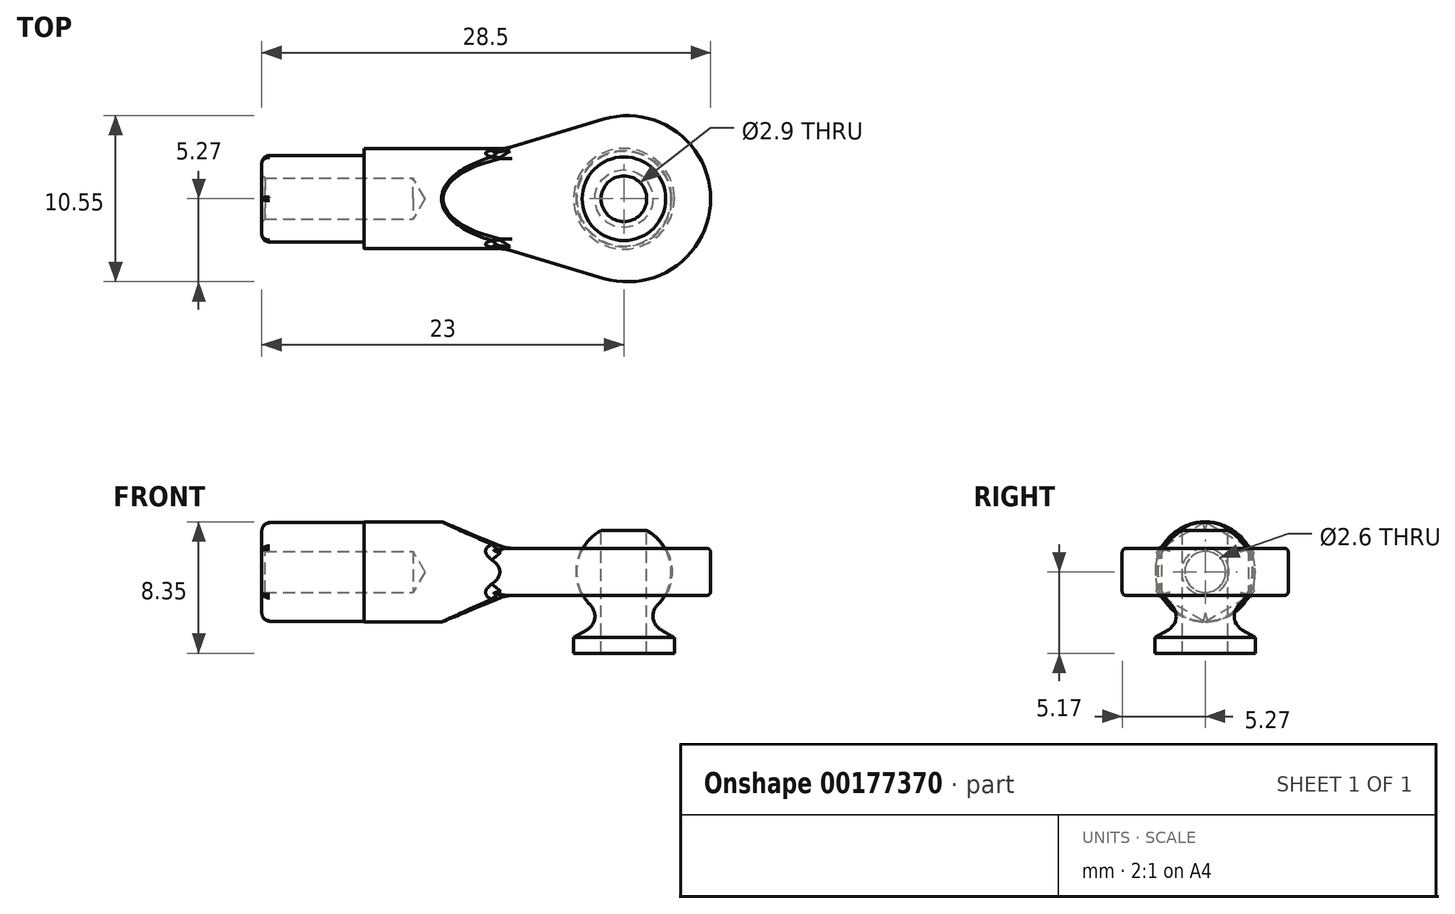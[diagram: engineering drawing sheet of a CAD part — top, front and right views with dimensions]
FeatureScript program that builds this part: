
annotation { "Feature Type Name" : "Feature", "Feature Type Description" : "" }
export const myFeature = defineFeature(function(context is Context, id is Id, definition is map)
    precondition{}
    {
        {
            var Q0;
            Q0=qCreatedBy(makeId("Right.planeOp"),FACE);
            var sketch = newSketch(context, id + "F0", { "sketchPlane" : qUnion([Q0])});
            skCircle(sketch, "E0.cCircle", {"center": v(0, 0) * mm, "radius": 2.75 * mm, "construction": true});
            skLineSegment(sketch, "E0.0", {"start": v(2.75, 1.59) * mm, "end": v(2.75, -1.59) * mm});
            skLineSegment(sketch, "E0.1", {"start": v(2.75, -1.59) * mm, "end": v(0, -3.18) * mm});
            skLineSegment(sketch, "E0.2", {"start": v(0, -3.18) * mm, "end": v(-2.75, -1.59) * mm});
            skLineSegment(sketch, "E0.3", {"start": v(-2.75, -1.59) * mm, "end": v(-2.75, 1.59) * mm});
            skLineSegment(sketch, "E0.4", {"start": v(-2.75, 1.59) * mm, "end": v(0, 3.18) * mm});
            skLineSegment(sketch, "E0.5", {"start": v(0, 3.18) * mm, "end": v(2.75, 1.59) * mm});
            skPoint(sketch, "E0.0.midPoint", {"position": v(2.75, 0) * mm});
            skSolve(sketch);
        }
        {
            var Q0;
            Q0 = qSketchRegion(id + "F0", true);
            extrude(context, id + "F1", {"entities" : qUnion([Q0]), "depth" : 6.5 * mm, "offsetDistance" : 25 * mm});
        }
        {
            var Q0;
            Q0=makeQuery(id+"F1.opExtrude","CAP_FACE",FACE,{"disambiguationData":[OSD([sQuery(id+"F0.wireOp",EDGE,"E0.0"),sQuery(id+"F0.wireOp",EDGE,"E0.1"),sQuery(id+"F0.wireOp",EDGE,"E0.2"),sQuery(id+"F0.wireOp",EDGE,"E0.3"),sQuery(id+"F0.wireOp",EDGE,"E0.4"),sQuery(id+"F0.wireOp",EDGE,"E0.5")])],"isStart":false});
            var sketch = newSketch(context, id + "F2", { "sketchPlane" : qUnion([Q0])});
            skCircle(sketch, "E1", {"center": v(0, 0) * mm, "radius": 3.18 * mm});
            skSolve(sketch);
        }
        {
            var Q0;
            Q0 = qSketchRegion(id + "F2", true);
            extrude(context, id + "F3", {"entities" : qUnion([Q0]), "operationType" : NewBodyOperationType.ADD, "depth" : 9 * mm, "offsetDistance" : 25 * mm});
        }
        {
            var Q0;
            Q0=qCreatedBy(makeId("Top.planeOp"),FACE);
            var sketch = newSketch(context, id + "F4", { "sketchPlane" : qUnion([Q0])});
            skCircle(sketch, "E2", {"center": v(23.23, 0) * mm, "radius": 5.28 * mm, "construction": true});
            skLineSegment(sketch, "E3", {"start": v(21.72, -5.05) * mm, "end": v(13.5, -2.6) * mm});
            skLineSegment(sketch, "E4", {"start": v(13.5, -2.6) * mm, "end": v(13.5, 2.6) * mm});
            skLineSegment(sketch, "E5", {"start": v(13.5, 2.6) * mm, "end": v(21.72, 5.05) * mm});
            skArc(sketch, "E6", {"start": v(21.72, -5.05) * mm, "mid": v(28.5, 0) * mm, "end": v(21.72, 5.05) * mm});
            skPoint(sketch, "E7", {"position": v(15.5, 3.2) * mm});
            skPoint(sketch, "E8", {"position": v(15.5, -3.2) * mm});
            skSolve(sketch);
        }
        {
            var Q0;
            Q0 = qSketchRegion(id + "F4", true);
            extrude(context, id + "F5", {"entities" : qUnion([Q0]), "operationType" : NewBodyOperationType.ADD, "depth" : 3 * mm, "offsetDistance" : 25 * mm, "symmetric" : true});
        }
        {
            var Q0;
            Q0=qCreatedBy(makeId("Front.planeOp"),FACE);
            var sketch = newSketch(context, id + "F6", { "sketchPlane" : qUnion([Q0])});
            skLineSegment(sketch, "E9", {"start": v(15.5, 1.5) * mm, "end": v(10.25, 3.67) * mm});
            skLineSegment(sketch, "E10", {"start": v(10.25, 3.67) * mm, "end": v(16.92, 3.67) * mm});
            skLineSegment(sketch, "E11", {"start": v(16.92, 3.67) * mm, "end": v(15.5, 1.5) * mm});
            skLineSegment(sketch, "E12", {"start": v(15.5, -1.5) * mm, "end": v(9.73, -3.9) * mm});
            skLineSegment(sketch, "E13", {"start": v(9.73, -3.9) * mm, "end": v(16.66, -3.9) * mm});
            skLineSegment(sketch, "E14", {"start": v(16.66, -3.9) * mm, "end": v(15.5, -1.5) * mm});
            skSolve(sketch);
        }
        {
            var Q0;
            Q0 = qSketchRegion(id + "F6", true);
            extrude(context, id + "F7", {"entities" : qUnion([Q0]), "operationType" : NewBodyOperationType.REMOVE, "oppositeDirection" : true, "depth" : 27.6 * mm, "offsetDistance" : 25 * mm, "symmetric" : true});
        }
        {
            var Q0;
            Q0=qCreatedBy(makeId("Front.planeOp"),FACE);
            var sketch = newSketch(context, id + "F8", { "sketchPlane" : qUnion([Q0])});
            skLineSegment(sketch, "E15", {"start": v(23, 3.05) * mm, "end": v(23, -3.05) * mm});
            skArc(sketch, "E16", {"start": v(23, 3.05) * mm, "mid": v(19.95, 0) * mm, "end": v(23, -3.05) * mm});
            skSolve(sketch);
        }
        {
            var Q0;
            Q0=makeQuery(id+"F8.imprint","IMPRINT",FACE,{"disambiguationData":[TD([[makeQuery(id+"F8.imprint","IMPRINT",EDGE,{"derivedFrom":sQuery(id+"F8.wireOp",EDGE,"E15")}),-1.0]])]});
            var Q1;
            Q1=sQuery(id+"F8.wireOp",EDGE,"E15");
            revolve(context, id + "F9", {"operationType" : NewBodyOperationType.REMOVE, "surfaceOperationType" : NewSurfaceOperationType.NEW, "entities" : qUnion([Q0]), "axis" : qUnion([Q1]), "revolveType" : RevolveType.FULL, "oppositeDirection" : true});
        }
        {
            var Q0;
            Q0=makeQuery(id+"F1.opExtrude","CAP_FACE",FACE,{"disambiguationData":[OSD([sQuery(id+"F0.wireOp",EDGE,"E0.0"),sQuery(id+"F0.wireOp",EDGE,"E0.1"),sQuery(id+"F0.wireOp",EDGE,"E0.2"),sQuery(id+"F0.wireOp",EDGE,"E0.3"),sQuery(id+"F0.wireOp",EDGE,"E0.4"),sQuery(id+"F0.wireOp",EDGE,"E0.5")])],"isStart":true});
            fillet(context, id + "F10", {"entities" : qUnion([Q0]), "radius" : 0.5 * mm, "tangentPropagation" : true, "allowEdgeOverflow" : false});
        }
        {
            var Q0;
            Q0=makeQuery(id+"F1.opExtrude","CAP_FACE",FACE,{"disambiguationData":[OSD([sQuery(id+"F0.wireOp",EDGE,"E0.0"),sQuery(id+"F0.wireOp",EDGE,"E0.1"),sQuery(id+"F0.wireOp",EDGE,"E0.2"),sQuery(id+"F0.wireOp",EDGE,"E0.3"),sQuery(id+"F0.wireOp",EDGE,"E0.4"),sQuery(id+"F0.wireOp",EDGE,"E0.5")])],"isStart":true});
            var sketch = newSketch(context, id + "F11", { "sketchPlane" : qUnion([Q0])});
            skPoint(sketch, "E17", {"position": v(0, 0) * mm});
            skSolve(sketch);
        }
        {
            var Q0;
            Q0=sQuery(id+"F11.wireOp",VERTEX,"E17");
            var Q1;
            Q1=makeQuery(id+"F1.opExtrude","SWEPT_BODY",BODY,{"disambiguationData":[OSD([sQuery(id+"F0.wireOp",EDGE,"E0.0"),sQuery(id+"F0.wireOp",EDGE,"E0.1"),sQuery(id+"F0.wireOp",EDGE,"E0.2"),sQuery(id+"F0.wireOp",EDGE,"E0.3"),sQuery(id+"F0.wireOp",EDGE,"E0.4"),sQuery(id+"F0.wireOp",EDGE,"E0.5")])]});
            hole(context, id + "F12", {"style" : HoleStyle.C_SINK, "endStyle" : HoleEndStyle.BLIND, "standardTappedOrClearance" : lookupTablePath({ "standard" : "ISO", "size" : "2.6", "type" : "Drilled" }), "standardBlindInLast" : lookupTablePath({ "standard" : "ISO", "size" : "2.6", "type" : "Drilled" }), "holeDiameter" : 2.6 * mm, "cSinkDiameter" : 3 * mm, "cSinkAngle" : 90 * degree, "majorDiameter" : 4 * mm, "holeDepth" : 9.6 * mm, "tappedDepth" : 7.5 * mm, "tapClearance" : 3, "locations" : qUnion([Q0]), "scope" : qUnion([Q1]), "startStyle" : HoleStartStyle.PART});
        }
        {
            var Q0;
            Q0=makeQuery(id+"F5.opExtrude","CAP_EDGE",EDGE,{"disambiguationData":[OSD([sQuery(id+"F4.wireOp",EDGE,"E3")])],"isStart":true});
            var Q1;
            Q1=makeQuery(id+"F5.opExtrude","CAP_EDGE",EDGE,{"disambiguationData":[OSD([sQuery(id+"F4.wireOp",EDGE,"E3")])],"isStart":false});
            var Q2;
            Q2=makeQuery(id+"F7.boolean.opBoolean","INTERSECT",EDGE,{"derivedFrom":[makeQuery(id+"F3.opExtrude","SWEPT_FACE",FACE,{"disambiguationData":[OSD([sQuery(id+"F2.wireOp",EDGE,"E1")])]}),makeQuery(id+"F7.opExtrude","SWEPT_FACE",FACE,{"disambiguationData":[OSD([sQuery(id+"F6.wireOp",EDGE,"E9")])]})]});
            var Q3;
            Q3=makeQuery(id+"F7.boolean.opBoolean","INTERSECT",EDGE,{"derivedFrom":[makeQuery(id+"F3.opExtrude","SWEPT_FACE",FACE,{"disambiguationData":[OSD([sQuery(id+"F2.wireOp",EDGE,"E1")])]}),makeQuery(id+"F7.opExtrude","SWEPT_FACE",FACE,{"disambiguationData":[OSD([sQuery(id+"F6.wireOp",EDGE,"E12")])]})]});
            fillet(context, id + "F13", {"entities" : qUnion([Q0, Q1, Q2, Q3]), "radius" : 0.25 * mm, "tangentPropagation" : true, "allowEdgeOverflow" : false});
        }
        {
            var Q0;
            Q0=makeQuery(id+"F7.boolean.opBoolean","MERGE",EDGE,{"derivedFrom":[makeQuery(id+"F5.boolean.opBoolean","INTERSECT",EDGE,{"derivedFrom":[makeQuery(id+"F3.opExtrude","CAP_FACE",FACE,{"disambiguationData":[OSD([sQuery(id+"F2.wireOp",EDGE,"E1")])],"isStart":false}),makeQuery(id+"F5.opExtrude","CAP_FACE",FACE,{"disambiguationData":[OSD([sQuery(id+"F4.wireOp",EDGE,"E3"),sQuery(id+"F4.wireOp",EDGE,"E4"),sQuery(id+"F4.wireOp",EDGE,"E5"),sQuery(id+"F4.wireOp",EDGE,"E6")])],"isStart":true})]})],"fromTools":[makeQuery(id+"F7.opExtrude","SWEPT_EDGE",EDGE,{"disambiguationData":[OSD([sQuery(id+"F6.wireOp",EDGE,"E12"),sQuery(id+"F6.wireOp",EDGE,"E14")])]})]});
            fillet(context, id + "F14", {"entities" : qUnion([Q0]), "radius" : 2 * mm, "tangentPropagation" : true, "allowEdgeOverflow" : false});
        }
        {
            var Q0;
            Q0=makeQuery(id+"F1.opExtrude","SWEPT_EDGE",EDGE,{"disambiguationData":[OSD([sQuery(id+"F0.wireOp",EDGE,"E0.4"),sQuery(id+"F0.wireOp",EDGE,"E0.5")])]});
            var Q1;
            Q1=makeQuery(id+"F1.opExtrude","SWEPT_EDGE",EDGE,{"disambiguationData":[OSD([sQuery(id+"F0.wireOp",EDGE,"E0.0"),sQuery(id+"F0.wireOp",EDGE,"E0.5")])]});
            var Q2;
            Q2=makeQuery(id+"F1.opExtrude","SWEPT_EDGE",EDGE,{"disambiguationData":[OSD([sQuery(id+"F0.wireOp",EDGE,"E0.0"),sQuery(id+"F0.wireOp",EDGE,"E0.1")])]});
            var Q3;
            Q3=makeQuery(id+"F1.opExtrude","SWEPT_EDGE",EDGE,{"disambiguationData":[OSD([sQuery(id+"F0.wireOp",EDGE,"E0.1"),sQuery(id+"F0.wireOp",EDGE,"E0.2")])]});
            var Q4;
            Q4=makeQuery(id+"F1.opExtrude","SWEPT_EDGE",EDGE,{"disambiguationData":[OSD([sQuery(id+"F0.wireOp",EDGE,"E0.2"),sQuery(id+"F0.wireOp",EDGE,"E0.3")])]});
            var Q5;
            Q5=makeQuery(id+"F1.opExtrude","SWEPT_EDGE",EDGE,{"disambiguationData":[OSD([sQuery(id+"F0.wireOp",EDGE,"E0.3"),sQuery(id+"F0.wireOp",EDGE,"E0.4")])]});
            fillet(context, id + "F15", {"entities" : qUnion([Q0, Q1, Q2, Q3, Q4, Q5]), "radius" : 0.25 * mm, "tangentPropagation" : true, "allowEdgeOverflow" : false});
        }
        {
            var Q0;
            Q0=qCreatedBy(makeId("Front.planeOp"),FACE);
            var sketch = newSketch(context, id + "F16", { "sketchPlane" : qUnion([Q0])});
            skLineSegment(sketch, "E18", {"start": v(23, 4.96) * mm, "end": v(23, -4.96) * mm, "construction": true});
            skLineSegment(sketch, "E19", {"start": v(21.55, 2.63) * mm, "end": v(21.55, -5.17) * mm});
            skCircle(sketch, "E20", {"center": v(23, 0) * mm, "radius": 3 * mm, "construction": true});
            skLineSegment(sketch, "E21", {"start": v(21.55, -5.17) * mm, "end": v(19.8, -5.17) * mm});
            skLineSegment(sketch, "E22", {"start": v(19.8, -5.17) * mm, "end": v(19.8, -4.17) * mm});
            skLineSegment(sketch, "E23", {"start": v(19.8, -4.17) * mm, "end": v(20.66, -3.68) * mm});
            skArc(sketch, "E24", {"start": v(20.66, -3.68) * mm, "mid": v(21.15, -2.95) * mm, "end": v(20.87, -2.1) * mm});
            skArc(sketch, "E25", {"start": v(21.55, 2.63) * mm, "mid": v(20.03, 0.43) * mm, "end": v(20.87, -2.1) * mm});
            skSolve(sketch);
        }
        {
            var Q0;
            Q0 = qSketchRegion(id + "F16", true);
            var Q1;
            Q1=sQuery(id+"F16.wireOp",EDGE,"E18");
            revolve(context, id + "F17", {"surfaceOperationType" : NewSurfaceOperationType.NEW, "entities" : qUnion([Q0]), "axis" : qUnion([Q1]), "revolveType" : RevolveType.FULL});
        }
    });
